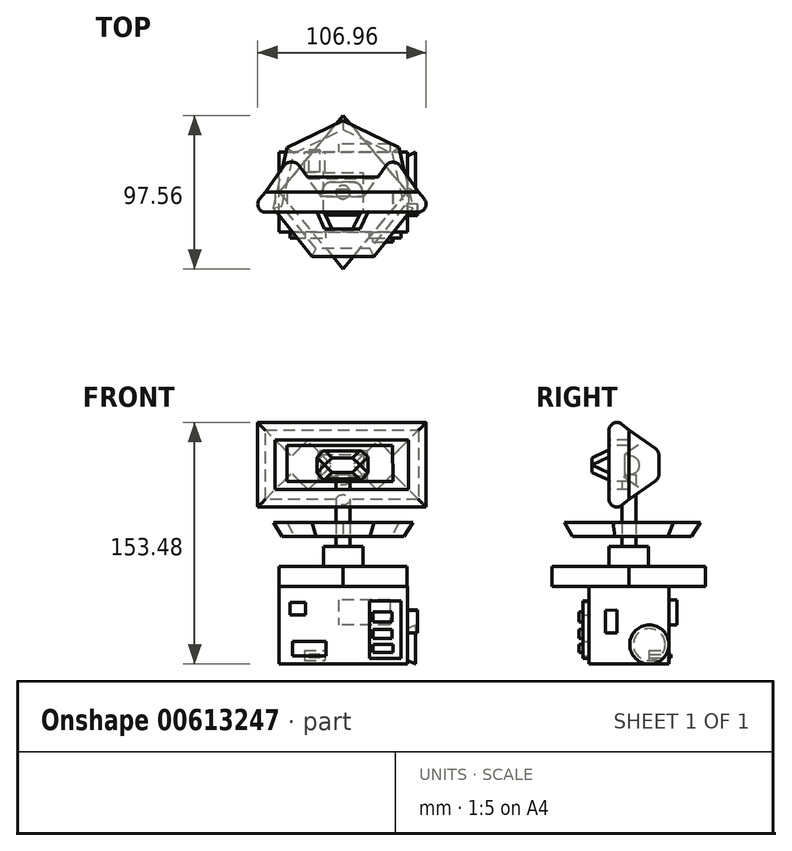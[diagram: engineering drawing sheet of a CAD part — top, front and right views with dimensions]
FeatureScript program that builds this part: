
annotation { "Feature Type Name" : "Feature", "Feature Type Description" : "" }
export const myFeature = defineFeature(function(context is Context, id is Id, definition is map)
    precondition{}
    {
        {
            var Q0;
            Q0=qCreatedBy(makeId("Top.planeOp"),FACE);
            var sketch = newSketch(context, id + "F0", { "sketchPlane" : qUnion([Q0])});
            skLineSegment(sketch, "E0", {"start": v(0, 48.78) * mm, "end": v(-40.72, 0) * mm});
            skLineSegment(sketch, "E1", {"start": v(0, 48.78) * mm, "end": v(40.72, 0) * mm});
            skLineSegment(sketch, "E2", {"start": v(40.72, 0) * mm, "end": v(-40.72, 0) * mm});
            skLineSegment(sketch, "E3", {"start": v(-40.72, 0) * mm, "end": v(0, -48.78) * mm});
            skLineSegment(sketch, "E4", {"start": v(0, -48.78) * mm, "end": v(40.72, 0) * mm});
            skSolve(sketch);
        }
        {
            var Q0;
            Q0=qCreatedBy(makeId("Front.planeOp"),FACE);
            var sketch = newSketch(context, id + "F1", { "sketchPlane" : qUnion([Q0])});
            skLineSegment(sketch, "E5", {"start": v(-40.72, 0) * mm, "end": v(-40.72, -49.31) * mm});
            skLineSegment(sketch, "E6", {"start": v(41, 0) * mm, "end": v(41, -49.31) * mm});
            skLineSegment(sketch, "E7", {"start": v(41, -49.31) * mm, "end": v(-40.72, -49.31) * mm});
            skLineSegment(sketch, "E8", {"start": v(-40.72, 0) * mm, "end": v(41, 0) * mm});
            skSolve(sketch);
        }
        {
            var Q0;
            Q0=makeQuery(id+"F1.imprint","IMPRINT",FACE,{"disambiguationData":[TD([[makeQuery(id+"F1.imprint","IMPRINT",EDGE,{"derivedFrom":sQuery(id+"F1.wireOp",EDGE,"E5")}),1.0]])]});
            extrude(context, id + "F2", {"entities" : qUnion([Q0]), "depth" : 25.4 * mm, "offsetDistance" : 25.4 * mm, "hasSecondDirection" : true, "secondDirectionOppositeDirection" : true, "secondDirectionDepth" : 25.4 * mm});
        }
        {
            var Q0;
            Q0 = qSketchRegion(id + "F0", true);
            extrude(context, id + "F3", {"entities" : qUnion([Q0]), "depth" : 12.7 * mm, "offsetDistance" : 25.4 * mm});
        }
        {
            var Q0;
            Q0=makeQuery(id+"F3.opExtrude","CAP_FACE",FACE,{"disambiguationData":[OSD([sQuery(id+"F0.wireOp",EDGE,"E0"),sQuery(id+"F0.wireOp",EDGE,"E1"),sQuery(id+"F0.wireOp",EDGE,"E3"),sQuery(id+"F0.wireOp",EDGE,"E4")])],"isStart":false});
            var sketch = newSketch(context, id + "F4", { "sketchPlane" : qUnion([Q0])});
            skCircle(sketch, "E9.cCircle", {"center": v(0, 0) * mm, "radius": 12.52 * mm, "construction": true});
            skLineSegment(sketch, "E9.0", {"start": v(-12.52, 12.52) * mm, "end": v(12.52, 12.52) * mm});
            skLineSegment(sketch, "E9.1", {"start": v(12.52, 12.52) * mm, "end": v(12.52, -12.52) * mm});
            skLineSegment(sketch, "E9.2", {"start": v(12.52, -12.52) * mm, "end": v(-12.52, -12.52) * mm});
            skLineSegment(sketch, "E9.3", {"start": v(-12.52, -12.52) * mm, "end": v(-12.52, 12.52) * mm});
            skPoint(sketch, "E9.0.midPoint", {"position": v(0, 12.52) * mm});
            skSolve(sketch);
        }
        {
            var Q0;
            Q0 = qSketchRegion(id + "F4", true);
            extrude(context, id + "F5", {"entities" : qUnion([Q0]), "depth" : 12.7 * mm, "offsetDistance" : 25.4 * mm});
        }
        {
            var Q0;
            Q0=makeQuery(id+"F2.opExtrude","SWEPT_FACE",FACE,{"disambiguationData":[OSD([sQuery(id+"F1.wireOp",EDGE,"E6")])]});
            var sketch = newSketch(context, id + "F6", { "sketchPlane" : qUnion([Q0])});
            skLineSegment(sketch, "E10", {"start": v(-14.82, -15.4) * mm, "end": v(-14.82, -29.79) * mm});
            skLineSegment(sketch, "E11", {"start": v(-14.82, -29.79) * mm, "end": v(-7.63, -29.79) * mm});
            skLineSegment(sketch, "E12", {"start": v(-7.63, -29.79) * mm, "end": v(-7.63, -15.1) * mm});
            skLineSegment(sketch, "E13", {"start": v(-7.63, -15.1) * mm, "end": v(-14.82, -15.4) * mm});
            skSolve(sketch);
        }
        {
            var Q0;
            Q0 = qSketchRegion(id + "F6", true);
            extrude(context, id + "F7", {"entities" : qUnion([Q0]), "depth" : 6.35 * mm, "offsetDistance" : 25.4 * mm});
        }
        {
            var Q0;
            Q0=makeQuery(id+"F2.opExtrude","CAP_FACE",FACE,{"disambiguationData":[OSD([sQuery(id+"F1.wireOp",EDGE,"E5"),sQuery(id+"F1.wireOp",EDGE,"E6"),sQuery(id+"F1.wireOp",EDGE,"E7"),sQuery(id+"F1.wireOp",EDGE,"E8")])],"isStart":true});
            var sketch = newSketch(context, id + "F8", { "sketchPlane" : qUnion([Q0])});
            skLineSegment(sketch, "E14.bottom", {"start": v(-29.8, -8.64) * mm, "end": v(2.94, -8.64) * mm});
            skLineSegment(sketch, "E14.top", {"start": v(-29.8, -24.54) * mm, "end": v(2.94, -24.54) * mm});
            skLineSegment(sketch, "E14.left", {"start": v(-29.8, -8.64) * mm, "end": v(-29.8, -24.54) * mm});
            skLineSegment(sketch, "E14.right", {"start": v(2.94, -8.64) * mm, "end": v(2.94, -24.54) * mm});
            skLineSegment(sketch, "E15.bottom", {"start": v(24.54, -40.7) * mm, "end": v(11.49, -40.7) * mm});
            skLineSegment(sketch, "E15.top", {"start": v(24.54, -47.23) * mm, "end": v(11.49, -47.23) * mm});
            skLineSegment(sketch, "E15.left", {"start": v(24.54, -40.7) * mm, "end": v(24.54, -47.23) * mm});
            skLineSegment(sketch, "E15.right", {"start": v(11.49, -40.7) * mm, "end": v(11.49, -47.23) * mm});
            skLineSegment(sketch, "E16.bottom", {"start": v(14.64, -43.18) * mm, "end": v(21.61, -43.18) * mm});
            skLineSegment(sketch, "E16.top", {"start": v(14.64, -45.43) * mm, "end": v(21.61, -45.43) * mm});
            skLineSegment(sketch, "E16.left", {"start": v(14.64, -43.18) * mm, "end": v(14.64, -45.43) * mm});
            skLineSegment(sketch, "E16.right", {"start": v(21.61, -43.18) * mm, "end": v(21.61, -45.43) * mm});
            skSolve(sketch);
        }
        {
            var Q0;
            Q0=makeQuery(id+"F8.imprint","IMPRINT",FACE,{"disambiguationData":[TD([[makeQuery(id+"F8.imprint","IMPRINT",EDGE,{"derivedFrom":sQuery(id+"F8.wireOp",EDGE,"E16.bottom")}),-1.0]])]});
            extrude(context, id + "F9", {"entities" : qUnion([Q0]), "depth" : 1.27 * mm, "offsetDistance" : 25.4 * mm});
        }
        {
            var Q0;
            Q0=makeQuery(id+"F8.imprint","IMPRINT",FACE,{"disambiguationData":[TD([[makeQuery(id+"F8.imprint","IMPRINT",EDGE,{"derivedFrom":sQuery(id+"F8.wireOp",EDGE,"E14.bottom")}),-1.0]])]});
            extrude(context, id + "F10", {"entities" : qUnion([Q0]), "depth" : 5.08 * mm, "offsetDistance" : 25.4 * mm});
        }
        {
            var Q0;
            Q0=makeQuery(id+"F8.imprint","IMPRINT",FACE,{"disambiguationData":[TD([[makeQuery(id+"F8.imprint","IMPRINT",EDGE,{"derivedFrom":sQuery(id+"F8.wireOp",EDGE,"E15.bottom")}),1.0]])]});
            extrude(context, id + "F11", {"entities" : qUnion([Q0]), "operationType" : NewBodyOperationType.REMOVE, "oppositeDirection" : true, "depth" : 12.7 * mm, "offsetDistance" : 25.4 * mm});
        }
        {
            var Q0;
            Q0=makeQuery(id+"F2.opExtrude","CAP_FACE",FACE,{"disambiguationData":[OSD([sQuery(id+"F1.wireOp",EDGE,"E5"),sQuery(id+"F1.wireOp",EDGE,"E6"),sQuery(id+"F1.wireOp",EDGE,"E7"),sQuery(id+"F1.wireOp",EDGE,"E8")])],"isStart":false});
            var sketch = newSketch(context, id + "F12", { "sketchPlane" : qUnion([Q0])});
            skLineSegment(sketch, "E17.bottom", {"start": v(-33.63, -10.24) * mm, "end": v(-23.95, -10.24) * mm});
            skLineSegment(sketch, "E17.top", {"start": v(-33.63, -18.34) * mm, "end": v(-23.95, -18.34) * mm});
            skLineSegment(sketch, "E17.left", {"start": v(-33.63, -10.24) * mm, "end": v(-33.63, -18.34) * mm});
            skLineSegment(sketch, "E17.right", {"start": v(-23.95, -10.24) * mm, "end": v(-23.95, -18.34) * mm});
            skLineSegment(sketch, "E18.bottom", {"start": v(-32.05, -35.22) * mm, "end": v(-10.68, -35.22) * mm});
            skLineSegment(sketch, "E18.top", {"start": v(-32.05, -44.22) * mm, "end": v(-10.68, -44.22) * mm});
            skLineSegment(sketch, "E18.left", {"start": v(-32.05, -35.22) * mm, "end": v(-32.05, -44.22) * mm});
            skLineSegment(sketch, "E18.right", {"start": v(-10.68, -35.22) * mm, "end": v(-10.68, -44.22) * mm});
            skLineSegment(sketch, "E19.bottom", {"start": v(16.77, -9.34) * mm, "end": v(36.8, -9.34) * mm});
            skLineSegment(sketch, "E19.top", {"start": v(16.77, -45.8) * mm, "end": v(36.8, -45.8) * mm});
            skLineSegment(sketch, "E19.left", {"start": v(16.77, -9.34) * mm, "end": v(16.77, -45.8) * mm});
            skLineSegment(sketch, "E19.right", {"start": v(36.8, -9.34) * mm, "end": v(36.8, -45.8) * mm});
            skSolve(sketch);
        }
        {
            var Q0;
            Q0=makeQuery(id+"F12.imprint","IMPRINT",FACE,{"disambiguationData":[TD([[makeQuery(id+"F12.imprint","IMPRINT",EDGE,{"derivedFrom":sQuery(id+"F12.wireOp",EDGE,"E17.bottom")}),-1.0]])]});
            var Q1;
            Q1=makeQuery(id+"F12.imprint","IMPRINT",FACE,{"disambiguationData":[TD([[makeQuery(id+"F12.imprint","IMPRINT",EDGE,{"derivedFrom":sQuery(id+"F12.wireOp",EDGE,"E18.bottom")}),-1.0]])]});
            var Q2;
            Q2=makeQuery(id+"F12.imprint","IMPRINT",FACE,{"disambiguationData":[TD([[makeQuery(id+"F12.imprint","IMPRINT",EDGE,{"derivedFrom":sQuery(id+"F12.wireOp",EDGE,"E19.bottom")}),-1.0]])]});
            extrude(context, id + "F13", {"entities" : qUnion([Q0, Q1, Q2]), "depth" : 3.8 * mm, "offsetDistance" : 25.4 * mm});
        }
        {
            var Q0;
            Q0=makeQuery(id+"F13.opExtrude","CAP_FACE",FACE,{"disambiguationData":[OSD([sQuery(id+"F12.wireOp",EDGE,"E19.bottom"),sQuery(id+"F12.wireOp",EDGE,"E19.top"),sQuery(id+"F12.wireOp",EDGE,"E19.left"),sQuery(id+"F12.wireOp",EDGE,"E19.right")])],"isStart":false});
            var sketch = newSketch(context, id + "F14", { "sketchPlane" : qUnion([Q0])});
            skLineSegment(sketch, "E20.bottom", {"start": v(19.1, -16.26) * mm, "end": v(31.2, -16.26) * mm});
            skLineSegment(sketch, "E20.top", {"start": v(19.1, -22.69) * mm, "end": v(31.2, -22.69) * mm});
            skLineSegment(sketch, "E20.left", {"start": v(19.1, -16.26) * mm, "end": v(19.1, -22.69) * mm});
            skLineSegment(sketch, "E20.right", {"start": v(31.2, -16.26) * mm, "end": v(31.2, -22.69) * mm});
            skLineSegment(sketch, "E21.bottom", {"start": v(19.1, -27.6) * mm, "end": v(31.01, -27.6) * mm});
            skLineSegment(sketch, "E21.top", {"start": v(19.1, -33.1) * mm, "end": v(31.01, -33.1) * mm});
            skLineSegment(sketch, "E21.left", {"start": v(19.1, -27.6) * mm, "end": v(19.1, -33.1) * mm});
            skLineSegment(sketch, "E21.right", {"start": v(31.01, -27.6) * mm, "end": v(31.01, -33.1) * mm});
            skLineSegment(sketch, "E22.bottom", {"start": v(19.1, -37.07) * mm, "end": v(31.58, -37.07) * mm});
            skLineSegment(sketch, "E22.top", {"start": v(19.1, -42.18) * mm, "end": v(31.58, -42.18) * mm});
            skLineSegment(sketch, "E22.left", {"start": v(19.1, -37.07) * mm, "end": v(19.1, -42.18) * mm});
            skLineSegment(sketch, "E22.right", {"start": v(31.58, -37.07) * mm, "end": v(31.58, -42.18) * mm});
            skSolve(sketch);
        }
        {
            var Q0;
            Q0=makeQuery(id+"F14.imprint","IMPRINT",FACE,{"disambiguationData":[TD([[makeQuery(id+"F14.imprint","IMPRINT",EDGE,{"derivedFrom":sQuery(id+"F14.wireOp",EDGE,"E20.bottom")}),-1.0]])]});
            var Q1;
            Q1=makeQuery(id+"F14.imprint","IMPRINT",FACE,{"disambiguationData":[TD([[makeQuery(id+"F14.imprint","IMPRINT",EDGE,{"derivedFrom":sQuery(id+"F14.wireOp",EDGE,"E21.bottom")}),-1.0]])]});
            var Q2;
            Q2=makeQuery(id+"F14.imprint","IMPRINT",FACE,{"disambiguationData":[TD([[makeQuery(id+"F14.imprint","IMPRINT",EDGE,{"derivedFrom":sQuery(id+"F14.wireOp",EDGE,"E22.bottom")}),-1.0]])]});
            extrude(context, id + "F15", {"entities" : qUnion([Q0, Q1, Q2]), "depth" : 2.54 * mm, "offsetDistance" : 25.4 * mm});
        }
        {
            var Q0;
            Q0=makeQuery(id+"F2.opExtrude","SWEPT_FACE",FACE,{"disambiguationData":[OSD([sQuery(id+"F1.wireOp",EDGE,"E6")])]});
            var sketch = newSketch(context, id + "F16", { "sketchPlane" : qUnion([Q0])});
            skCircle(sketch, "E23", {"center": v(12.97, -37.05) * mm, "radius": 10.07 * mm});
            skSolve(sketch);
        }
        {
            var Q0;
            Q0 = qSketchRegion(id + "F16", true);
            extrude(context, id + "F17", {"entities" : qUnion([Q0]), "depth" : 5.08 * mm, "offsetDistance" : 25.4 * mm, "hasDraft" : true, "draftAngle" : 25 * degree});
        }
        {
            var Q0;
            Q0=makeQuery(id+"F5.opExtrude","CAP_FACE",FACE,{"disambiguationData":[OSD([sQuery(id+"F4.wireOp",EDGE,"E9.0"),sQuery(id+"F4.wireOp",EDGE,"E9.1"),sQuery(id+"F4.wireOp",EDGE,"E9.2"),sQuery(id+"F4.wireOp",EDGE,"E9.3")])],"isStart":false});
            var sketch = newSketch(context, id + "F18", { "sketchPlane" : qUnion([Q0])});
            skCircle(sketch, "E24", {"center": v(0, 0) * mm, "radius": 4.35 * mm});
            skSolve(sketch);
        }
        {
            var Q0;
            Q0=makeQuery(id+"F18.imprint","IMPRINT",FACE,{"disambiguationData":[TD([[makeQuery(id+"F18.imprint","IMPRINT",EDGE,{"derivedFrom":sQuery(id+"F18.wireOp",EDGE,"E24")}),1.0]])]});
            extrude(context, id + "F19", {"entities" : qUnion([Q0]), "depth" : 6.35 * mm, "offsetDistance" : 25.4 * mm});
        }
        {
            var Q0;
            Q0=makeQuery(id+"F19.opExtrude","CAP_FACE",FACE,{"disambiguationData":[OSD([sQuery(id+"F18.wireOp",EDGE,"E24")])],"isStart":false});
            var sketch = newSketch(context, id + "F20", { "sketchPlane" : qUnion([Q0])});
            skCircle(sketch, "E25.cCircle", {"center": v(0, 0) * mm, "radius": 35.83 * mm, "construction": true});
            skLineSegment(sketch, "E25.0", {"start": v(17.26, -35.83) * mm, "end": v(-17.26, -35.83) * mm});
            skLineSegment(sketch, "E25.1", {"start": v(-17.26, -35.83) * mm, "end": v(-38.77, -8.85) * mm});
            skLineSegment(sketch, "E25.2", {"start": v(-38.77, -8.85) * mm, "end": v(-31.1, 24.8) * mm});
            skLineSegment(sketch, "E25.3", {"start": v(-31.1, 24.8) * mm, "end": v(0, 39.77) * mm});
            skLineSegment(sketch, "E25.4", {"start": v(0, 39.77) * mm, "end": v(31.1, 24.8) * mm});
            skLineSegment(sketch, "E25.5", {"start": v(31.1, 24.8) * mm, "end": v(38.77, -8.85) * mm});
            skLineSegment(sketch, "E25.6", {"start": v(38.77, -8.85) * mm, "end": v(17.26, -35.83) * mm});
            skPoint(sketch, "E25.0.midPoint", {"position": v(0, -35.83) * mm});
            skSolve(sketch);
        }
        {
            var Q0;
            Q0=makeQuery(id+"F19.opExtrude","CAP_FACE",FACE,{"disambiguationData":[OSD([sQuery(id+"F18.wireOp",EDGE,"E24")])],"isStart":false});
            var sketch = newSketch(context, id + "F21", { "sketchPlane" : qUnion([Q0])});
            skCircle(sketch, "E26", {"center": v(0, 0) * mm, "radius": 4.35 * mm});
            skSolve(sketch);
        }
        {
            var Q0;
            Q0 = qSketchRegion(id + "F21", true);
            extrude(context, id + "F22", {"entities" : qUnion([Q0]), "operationType" : NewBodyOperationType.ADD, "depth" : 13.97 * mm, "offsetDistance" : 25.4 * mm});
        }
        {
            var Q0;
            Q0 = qSketchRegion(id + "F20", true);
            extrude(context, id + "F23", {"entities" : qUnion([Q0]), "depth" : 8.9 * mm, "offsetDistance" : 25.4 * mm, "hasDraft" : true, "draftAngle" : 30 * degree});
        }
        {
            var Q0;
            Q0=qCreatedBy(makeId("Front.planeOp"),FACE);
            var sketch = newSketch(context, id + "F24", { "sketchPlane" : qUnion([Q0])});
            skLineSegment(sketch, "E27", {"start": v(-49.36, 99.15) * mm, "end": v(-49.36, 55.11) * mm});
            skLineSegment(sketch, "E28", {"start": v(-49.36, 55.11) * mm, "end": v(47.92, 55.11) * mm});
            skLineSegment(sketch, "E29", {"start": v(47.92, 55.11) * mm, "end": v(47.92, 99.15) * mm});
            skLineSegment(sketch, "E30", {"start": v(-49.36, 99.15) * mm, "end": v(47.92, 99.15) * mm});
            skLineSegment(sketch, "E31", {"start": v(-16.06, 85.82) * mm, "end": v(-16.06, 67.27) * mm});
            skLineSegment(sketch, "E32", {"start": v(-16.06, 67.27) * mm, "end": v(15.4, 67.27) * mm});
            skLineSegment(sketch, "E33", {"start": v(15.4, 67.27) * mm, "end": v(15.4, 85.82) * mm});
            skLineSegment(sketch, "E34", {"start": v(15.4, 85.82) * mm, "end": v(-16.06, 85.82) * mm});
            skSolve(sketch);
        }
        {
            var Q0;
            Q0=makeQuery(id+"F24.imprint","IMPRINT",FACE,{"disambiguationData":[TD([[makeQuery(id+"F24.imprint","IMPRINT",EDGE,{"derivedFrom":sQuery(id+"F24.wireOp",EDGE,"E27")}),1.0]])]});
            extrude(context, id + "F25", {"entities" : qUnion([Q0]), "depth" : 12.7 * mm, "offsetDistance" : 25.4 * mm, "hasDraft" : true, "draftAngle" : 40 * degree, "hasSecondDirection" : true, "secondDirectionOppositeDirection" : true, "secondDirectionDepth" : 19.05 * mm, "hasSecondDirectionDraft" : true, "secondDirectionDraftAngle" : 35 * degree, "secondDirectionDraftPullDirection" : true});
        }
        {
            var Q0;
            Q0=makeQuery(id+"F25.opExtrude","CAP_FACE",FACE,{"disambiguationData":[OSD([sQuery(id+"F24.wireOp",EDGE,"E27"),sQuery(id+"F24.wireOp",EDGE,"E28"),sQuery(id+"F24.wireOp",EDGE,"E29"),sQuery(id+"F24.wireOp",EDGE,"E30"),sQuery(id+"F24.wireOp",EDGE,"E31"),sQuery(id+"F24.wireOp",EDGE,"E32"),sQuery(id+"F24.wireOp",EDGE,"E33"),sQuery(id+"F24.wireOp",EDGE,"E34")])],"isStart":false});
            var sketch = newSketch(context, id + "F26", { "sketchPlane" : qUnion([Q0])});
            skLineSegment(sketch, "E35", {"start": v(-16.69, 86.53) * mm, "end": v(-16.69, 67.21) * mm});
            skLineSegment(sketch, "E36", {"start": v(-16.69, 67.21) * mm, "end": v(15.98, 67.21) * mm});
            skLineSegment(sketch, "E37", {"start": v(-16.69, 86.53) * mm, "end": v(15.63, 86.53) * mm});
            skLineSegment(sketch, "E38", {"start": v(15.63, 86.53) * mm, "end": v(15.98, 67.21) * mm});
            skSolve(sketch);
        }
        {
            var Q0;
            Q0=makeQuery(id+"F26.imprint","IMPRINT",FACE,{"disambiguationData":[TD([[makeQuery(id+"F26.imprint","IMPRINT",EDGE,{"derivedFrom":sQuery(id+"F26.wireOp",EDGE,"E35")}),1.0]])]});
            extrude(context, id + "F27", {"entities" : qUnion([Q0]), "depth" : 25.4 * mm, "offsetDistance" : 25.4 * mm, "hasDraft" : true, "draftAngle" : 25 * degree, "draftPullDirection" : true, "hasSecondDirection" : true, "secondDirectionOppositeDirection" : true, "secondDirectionDepth" : 19.05 * mm, "hasSecondDirectionDraft" : true, "secondDirectionDraftAngle" : 15 * degree, "secondDirectionDraftPullDirection" : true});
        }
        {
            var Q0;
            Q0=makeQuery(id+"F25.opExtrude","CAP_FACE",FACE,{"disambiguationData":[OSD([sQuery(id+"F24.wireOp",EDGE,"E27"),sQuery(id+"F24.wireOp",EDGE,"E28"),sQuery(id+"F24.wireOp",EDGE,"E29"),sQuery(id+"F24.wireOp",EDGE,"E30"),sQuery(id+"F24.wireOp",EDGE,"E31"),sQuery(id+"F24.wireOp",EDGE,"E32"),sQuery(id+"F24.wireOp",EDGE,"E33"),sQuery(id+"F24.wireOp",EDGE,"E34")])],"isStart":false});
            var Q1;
            Q1=makeQuery(id+"F27.opExtrude","CAP_FACE",FACE,{"disambiguationData":[OSD([sQuery(id+"F26.wireOp",EDGE,"E35"),sQuery(id+"F26.wireOp",EDGE,"E36"),sQuery(id+"F26.wireOp",EDGE,"E37"),sQuery(id+"F26.wireOp",EDGE,"E38")])],"isStart":true});
            var Q2;
            Q2=makeQuery(id+"F25.*.draftSecond.opDraft","SPLIT",FACE,{"disambiguationData":[OD(1.0)],"derivedFrom":makeQuery(id+"F25.opExtrude","CAP_FACE",FACE,{"disambiguationData":[OSD([sQuery(id+"F24.wireOp",EDGE,"E27"),sQuery(id+"F24.wireOp",EDGE,"E28"),sQuery(id+"F24.wireOp",EDGE,"E29"),sQuery(id+"F24.wireOp",EDGE,"E30"),sQuery(id+"F24.wireOp",EDGE,"E31"),sQuery(id+"F24.wireOp",EDGE,"E32"),sQuery(id+"F24.wireOp",EDGE,"E33"),sQuery(id+"F24.wireOp",EDGE,"E34")])],"isStart":true})});
            var Q3;
            Q3=makeQuery(id+"F25.*.draftSecond.opDraft","SPLIT",FACE,{"disambiguationData":[OD(0.0)],"derivedFrom":makeQuery(id+"F25.opExtrude","CAP_FACE",FACE,{"disambiguationData":[OSD([sQuery(id+"F24.wireOp",EDGE,"E27"),sQuery(id+"F24.wireOp",EDGE,"E28"),sQuery(id+"F24.wireOp",EDGE,"E29"),sQuery(id+"F24.wireOp",EDGE,"E30"),sQuery(id+"F24.wireOp",EDGE,"E31"),sQuery(id+"F24.wireOp",EDGE,"E32"),sQuery(id+"F24.wireOp",EDGE,"E33"),sQuery(id+"F24.wireOp",EDGE,"E34")])],"isStart":true})});
            fillet(context, id + "F28", {"entities" : qUnion([Q0, Q1, Q2, Q3]), "radius" : 5.08 * mm, "tangentPropagation" : true, "allowEdgeOverflow" : false});
        }
        {
            var Q0;
            Q0=makeQuery(id+"F27.*.split.splitOp","SPLIT",FACE,{"derivedFrom":makeQuery(id+"F27.opExtrude","SWEPT_FACE",FACE,{"disambiguationData":[OSD([sQuery(id+"F26.wireOp",EDGE,"E37")])]})});
            var Q1;
            Q1=makeQuery(id+"F27.*.split.splitOp","SPLIT",FACE,{"derivedFrom":makeQuery(id+"F27.opExtrude","SWEPT_FACE",FACE,{"disambiguationData":[OSD([sQuery(id+"F26.wireOp",EDGE,"E36")])]})});
            chamfer(context, id + "F29", {"entities" : qUnion([Q0, Q1]), "width" : 5.08 * mm, "tangentPropagation" : true});
        }
        {
            var Q0;
            Q0=makeQuery(id+"F25.opExtrude","CAP_FACE",FACE,{"disambiguationData":[OSD([sQuery(id+"F24.wireOp",EDGE,"E27"),sQuery(id+"F24.wireOp",EDGE,"E28"),sQuery(id+"F24.wireOp",EDGE,"E29"),sQuery(id+"F24.wireOp",EDGE,"E30"),sQuery(id+"F24.wireOp",EDGE,"E31"),sQuery(id+"F24.wireOp",EDGE,"E32"),sQuery(id+"F24.wireOp",EDGE,"E33"),sQuery(id+"F24.wireOp",EDGE,"E34")])],"isStart":false});
            var sketch = newSketch(context, id + "F30", { "sketchPlane" : qUnion([Q0])});
            skLineSegment(sketch, "E39", {"start": v(-43.13, 61.52) * mm, "end": v(41.55, 61.52) * mm});
            skLineSegment(sketch, "E40", {"start": v(41.55, 61.52) * mm, "end": v(41.55, 92.88) * mm});
            skLineSegment(sketch, "E41", {"start": v(31.64, 66.55) * mm, "end": v(31.37, 89.28) * mm});
            skLineSegment(sketch, "E42", {"start": v(41.55, 92.88) * mm, "end": v(-43.13, 92.88) * mm});
            skLineSegment(sketch, "E43", {"start": v(-43.13, 92.88) * mm, "end": v(-43.13, 61.52) * mm});
            skLineSegment(sketch, "E44", {"start": v(31.37, 89.28) * mm, "end": v(-35.51, 89.28) * mm});
            skLineSegment(sketch, "E45", {"start": v(-35.51, 89.28) * mm, "end": v(-35.51, 66.55) * mm});
            skLineSegment(sketch, "E46", {"start": v(-35.51, 66.55) * mm, "end": v(31.64, 66.55) * mm});
            skSolve(sketch);
        }
        {
            var Q0;
            Q0=makeQuery(id+"F30.imprint","IMPRINT",FACE,{"disambiguationData":[TD([[makeQuery(id+"F30.imprint","IMPRINT",EDGE,{"derivedFrom":sQuery(id+"F30.wireOp",EDGE,"E39")}),1.0]])]});
            extrude(context, id + "F31", {"entities" : qUnion([Q0]), "operationType" : NewBodyOperationType.REMOVE, "oppositeDirection" : true, "depth" : 12.7 * mm, "offsetDistance" : 25.4 * mm});
        }
        {
            var Q0;
            Q0=makeQuery(id+"F22.opExtrude","CAP_FACE",FACE,{"disambiguationData":[OSD([sQuery(id+"F21.wireOp",EDGE,"E26")])],"isStart":false});
            var sketch = newSketch(context, id + "F32", { "sketchPlane" : qUnion([Q0])});
            skCircle(sketch, "E47", {"center": v(0, 0) * mm, "radius": 4.47 * mm});
            skSolve(sketch);
        }
        {
            var Q0;
            Q0=makeQuery(id+"F32.imprint","IMPRINT",FACE,{"disambiguationData":[TD([[makeQuery(id+"F32.imprint","IMPRINT",EDGE,{"derivedFrom":makeQuery(id+"F22.opExtrude","CAP_EDGE",EDGE,{"disambiguationData":[OSD([sQuery(id+"F21.wireOp",EDGE,"E26")])],"isStart":false})}),1.0]])]});
            extrude(context, id + "F33", {"entities" : qUnion([Q0]), "operationType" : NewBodyOperationType.ADD, "depth" : 25.4 * mm, "offsetDistance" : 25.4 * mm});
        }
    });
